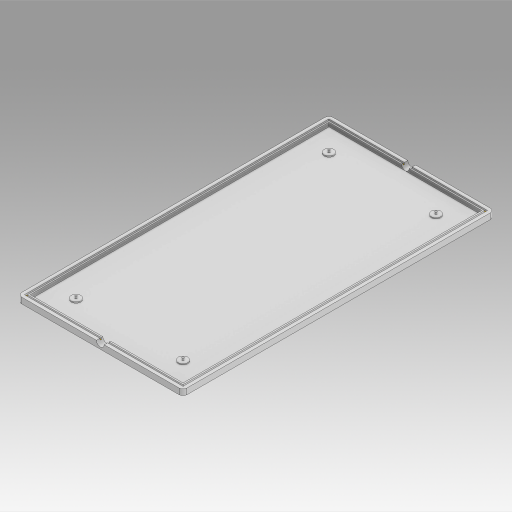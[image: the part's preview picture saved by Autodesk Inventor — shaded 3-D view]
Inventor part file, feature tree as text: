
AUTODESK INVENTOR PART (.ipt)
format: ipt  version: 2023 (Build 270158000, 158)  size: 251,392 bytes
history: native  units: in
note: dims shown in document units (in); Inventor stores cm internally (conversion verified against a paired STEP export)
features: extrude x6, sketch x4, fillet x1, projected_geometry x1
ambient origin geometry x8: Origin, YZ Plane, XZ Plane, XY Plane, X Axis, Y Axis, Z Axis, Center Point
bodies: Solid1 (feature_tree)
feature tree (12):
  extrude  "Extrusion1"  Depth=6.2992in
  fillet  "Fillet1"  Radius=0.1181in
  sketch  "Sketch2"  dims[d4=0.0787in d5=0.0984in]
  extrude  "Extrusion2"  Depth=0.0984in
  extrude  "Extrusion3"  Depth=0.0787in TaperAngle=0.0deg
  sketch  "Sketch3"  dims[d6=0.0295in d7=0.0787in d8=0.0in]
  extrude  "Extrusion4"  Depth=0.0295in
  extrude  "Extrusion5"  Depth=0.0295in
  extrude  "Extrusion6"  Depth=0.0295in
  sketch  "Sketch1"  dims[d0=3.3465in d1=6.2992in d2=0.1181in d3=0.0in]
  projected_geometry  "Projected Loop1"
  sketch  "Sketch4"  dims[d9=0.0295in d10=0.0in d11=0.1969in d12=0.1969in d13=0.1969in d14=0.1969in d15=0.0787in d16=0.0787in d17=0.0787in d18=0.0787in d19=0.5906in d20=0.5906in d21=0.5906in d22=0.5906in d23=0.5906in d24=0.5906in d25=0.5906in d26=0.5906in d27=0.0591in d28=0.0in d29=0.0197in d30=0.0in d31=0.0295in d32=1.6732in d33=0.1181in d34=0.0295in d35=0.0in]
